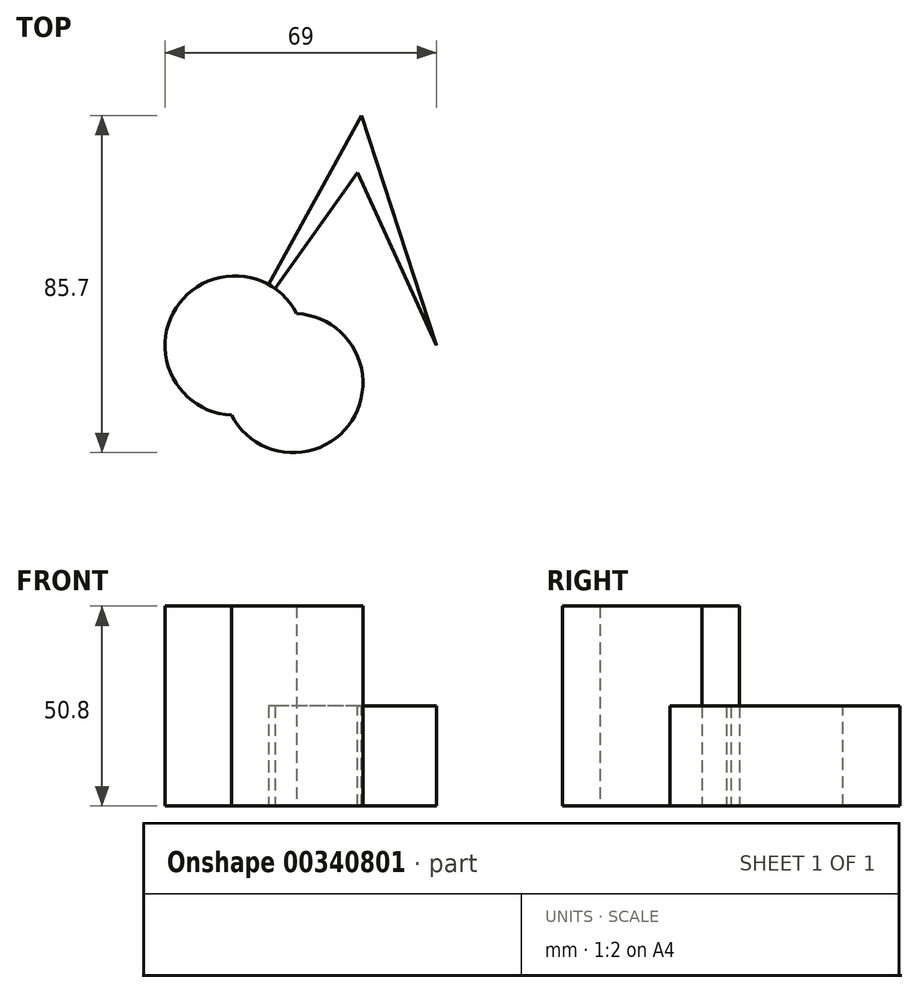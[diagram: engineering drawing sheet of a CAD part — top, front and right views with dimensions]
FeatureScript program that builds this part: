
annotation { "Feature Type Name" : "Feature", "Feature Type Description" : "" }
export const myFeature = defineFeature(function(context is Context, id is Id, definition is map)
    precondition{}
    {
        {
            var Q0;
            Q0=qCreatedBy(makeId("Top.planeOp"),FACE);
            var sketch = newSketch(context, id + "F0", { "sketchPlane" : qUnion([Q0])});
            skCircle(sketch, "E0", {"center": v(14.88, -9.54) * mm, "radius": 17.68 * mm});
            skCircle(sketch, "E1", {"center": v(0, 0) * mm, "radius": 17.71 * mm});
            skSolve(sketch);
        }
        {
            var Q0;
            Q0 = qSketchRegion(id + "F0", true);
            extrude(context, id + "F1", {"entities" : qUnion([Q0]), "endBound" : BoundingType.SYMMETRIC, "depth" : 50.8 * mm});
        }
        {
            var Q0;
            Q0=qCreatedBy(makeId("Top.planeOp"),FACE);
            var sketch = newSketch(context, id + "F2", { "sketchPlane" : qUnion([Q0])});
            skLineSegment(sketch, "E2", {"start": v(31.2, 43.94) * mm, "end": v(0, 0) * mm});
            skLineSegment(sketch, "E3", {"start": v(31.2, 43.94) * mm, "end": v(51.3, 0) * mm});
            skLineSegment(sketch, "E4", {"start": v(51.3, 0) * mm, "end": v(32.26, 58.48) * mm});
            skLineSegment(sketch, "E5", {"start": v(32.26, 58.48) * mm, "end": v(0, 0) * mm});
            skSolve(sketch);
        }
        {
            var Q0;
            Q0 = qSketchRegion(id + "F2", true);
            extrude(context, id + "F3", {"entities" : qUnion([Q0]), "operationType" : NewBodyOperationType.ADD, "oppositeDirection" : true, "depth" : 25.4 * mm});
        }
    });
